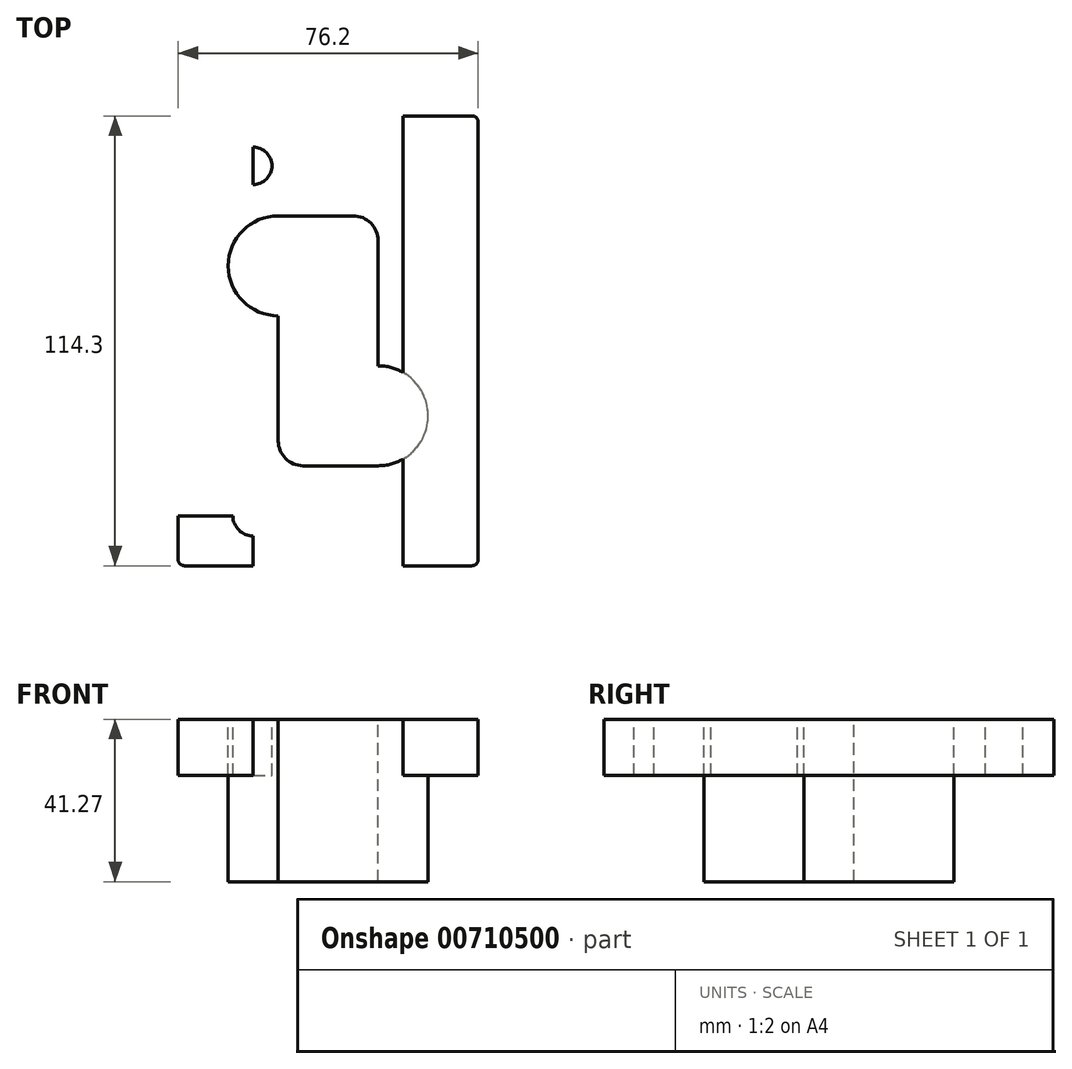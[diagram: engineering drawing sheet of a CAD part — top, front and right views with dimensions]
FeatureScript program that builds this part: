
annotation { "Feature Type Name" : "Feature", "Feature Type Description" : "" }
export const myFeature = defineFeature(function(context is Context, id is Id, definition is map)
    precondition{}
    {
        {
            var Q0;
            Q0=qCreatedBy(makeId("Top.planeOp"),FACE);
            var sketch = newSketch(context, id + "F0", { "sketchPlane" : qUnion([Q0])});
            skLineSegment(sketch, "E0.bottom", {"start": v(12.7, -31.75) * mm, "end": v(-6.35, -31.75) * mm});
            skLineSegment(sketch, "E0.top", {"start": v(6.35, 31.75) * mm, "end": v(-12.7, 31.75) * mm});
            skLineSegment(sketch, "E0.right", {"start": v(-12.7, -25.4) * mm, "end": v(-12.7, 6.35) * mm});
            skPoint(sketch, "E0.middle", {"position": v(0, 0) * mm});
            skArc(sketch, "E1", {"start": v(-12.7, 31.75) * mm, "mid": v(-25.4, 19.05) * mm, "end": v(-12.7, 6.35) * mm});
            skArc(sketch, "E2", {"start": v(12.7, -31.75) * mm, "mid": v(25.4, -19.05) * mm, "end": v(12.7, -6.35) * mm});
            skLineSegment(sketch, "E3.trimOffspring", {"start": v(12.7, -6.35) * mm, "end": v(12.7, 25.4) * mm});
            skPoint(sketch, "E4.start.orphan", {"position": v(-12.7, -19.05) * mm});
            skPoint(sketch, "E5.MirrorCS.end.orphan", {"position": v(12.7, 19.05) * mm});
            skPoint(sketch, "E6.visualSharp", {"position": v(-12.7, -31.75) * mm});
            skArc(sketch, "E6.filletArc", {"start": v(-12.7, -25.4) * mm, "mid": v(-10.84, -29.9) * mm, "end": v(-6.35, -31.75) * mm});
            skPoint(sketch, "E7.visualSharp", {"position": v(12.7, 31.75) * mm});
            skArc(sketch, "E7.filletArc", {"start": v(12.7, 25.4) * mm, "mid": v(10.84, 29.9) * mm, "end": v(6.35, 31.75) * mm});
            skPoint(sketch, "E8.visualSharp", {"position": v(6.35, 19.05) * mm});
            skPoint(sketch, "E9.visualSharp", {"position": v(6.35, -19.05) * mm});
            skSolve(sketch);
        }
        {
            var Q0;
            Q0=makeQuery(id+"F0.imprint","IMPRINT",FACE,{"disambiguationData":[TD([[makeQuery(id+"F0.imprint","IMPRINT",EDGE,{"derivedFrom":sQuery(id+"F0.wireOp",EDGE,"E0.bottom")}),-1.0]])]});
            extrude(context, id + "F1", {"entities" : qUnion([Q0]), "depth" : -41.27 * mm, "offsetDistance" : 25.4 * mm});
        }
        {
            var Q0;
            Q0=makeQuery(id+"F0.imprint","IMPRINT",FACE,{"disambiguationData":[TD([[makeQuery(id+"F0.imprint","IMPRINT",EDGE,{"derivedFrom":sQuery(id+"F0.wireOp",EDGE,"E0.bottom")}),-1.0]])]});
            var sketch = newSketch(context, id + "F2", { "sketchPlane" : qUnion([Q0])});
            skLineSegment(sketch, "E10.bottom", {"start": v(36.51, -57.15) * mm, "end": v(-36.51, -57.15) * mm});
            skLineSegment(sketch, "E10.top", {"start": v(36.51, 57.15) * mm, "end": v(-36.51, 57.15) * mm});
            skLineSegment(sketch, "E10.left", {"start": v(38.1, -55.56) * mm, "end": v(38.1, 55.56) * mm});
            skLineSegment(sketch, "E10.right", {"start": v(-38.1, -55.56) * mm, "end": v(-38.1, 55.56) * mm});
            skPoint(sketch, "E10.middle", {"position": v(0, 0) * mm});
            skLineSegment(sketch, "E11.0.0", {"start": v(6.35, 31.75) * mm, "end": v(-12.7, 31.75) * mm});
            skArc(sketch, "E11.0.1", {"start": v(-12.7, 31.75) * mm, "mid": v(-25.4, 19.05) * mm, "end": v(-12.7, 6.35) * mm});
            skLineSegment(sketch, "E11.0.2", {"start": v(-12.7, 6.35) * mm, "end": v(-12.7, -25.4) * mm});
            skArc(sketch, "E11.0.3", {"start": v(-12.7, -25.4) * mm, "mid": v(-10.84, -29.9) * mm, "end": v(-6.35, -31.75) * mm});
            skLineSegment(sketch, "E11.0.4", {"start": v(-6.35, -31.75) * mm, "end": v(12.7, -31.75) * mm});
            skArc(sketch, "E11.0.5", {"start": v(12.7, -31.75) * mm, "mid": v(25.4, -19.05) * mm, "end": v(12.7, -6.35) * mm});
            skLineSegment(sketch, "E11.0.6", {"start": v(12.7, -6.35) * mm, "end": v(12.7, 25.4) * mm});
            skArc(sketch, "E11.0.7", {"start": v(12.7, 25.4) * mm, "mid": v(10.84, 29.9) * mm, "end": v(6.35, 31.75) * mm});
            skPoint(sketch, "E12.visualSharp", {"position": v(-38.1, 57.15) * mm});
            skArc(sketch, "E12.filletArc", {"start": v(-36.51, 57.15) * mm, "mid": v(-37.64, 56.69) * mm, "end": v(-38.1, 55.56) * mm});
            skPoint(sketch, "E13.visualSharp", {"position": v(38.1, 57.15) * mm});
            skArc(sketch, "E13.filletArc", {"start": v(38.1, 55.56) * mm, "mid": v(37.64, 56.69) * mm, "end": v(36.51, 57.15) * mm});
            skPoint(sketch, "E14.visualSharp", {"position": v(38.1, -57.15) * mm});
            skArc(sketch, "E14.filletArc", {"start": v(36.51, -57.15) * mm, "mid": v(37.64, -56.69) * mm, "end": v(38.1, -55.56) * mm});
            skPoint(sketch, "E15.visualSharp", {"position": v(-38.1, -57.15) * mm});
            skArc(sketch, "E15.filletArc", {"start": v(-38.1, -55.56) * mm, "mid": v(-37.64, -56.69) * mm, "end": v(-36.51, -57.15) * mm});
            skSolve(sketch);
        }
        {
            var Q0;
            Q0=qSketchRegion(id+"F2",true);
            extrude(context, id + "F3", {"entities" : qUnion([Q0]), "operationType" : NewBodyOperationType.ADD, "depth" : -14.29 * mm, "offsetDistance" : 25.4 * mm});
        }
        {
            var Q0;
            Q0=makeQuery(id+"F2.imprint","IMPRINT",FACE,{"disambiguationData":[TD([[makeQuery(id+"F2.imprint","IMPRINT",EDGE,{"derivedFrom":sQuery(id+"F2.wireOp",EDGE,"E10.bottom")}),-1.0]])]});
            var sketch = newSketch(context, id + "F4", { "sketchPlane" : qUnion([Q0])});
            skArc(sketch, "E16.0.0", {"start": v(38.1, 55.56) * mm, "mid": v(37.64, 56.69) * mm, "end": v(36.51, 57.15) * mm});
            skLineSegment(sketch, "E16.0.1", {"start": v(36.51, 57.15) * mm, "end": v(-36.51, 57.15) * mm});
            skArc(sketch, "E16.0.2", {"start": v(-36.51, 57.15) * mm, "mid": v(-37.64, 56.69) * mm, "end": v(-38.1, 55.56) * mm});
            skLineSegment(sketch, "E16.0.3", {"start": v(-38.1, 55.56) * mm, "end": v(-38.1, -55.56) * mm});
            skArc(sketch, "E16.0.4", {"start": v(-38.1, -55.56) * mm, "mid": v(-37.64, -56.69) * mm, "end": v(-36.51, -57.15) * mm});
            skLineSegment(sketch, "E16.0.5", {"start": v(-36.51, -57.15) * mm, "end": v(36.51, -57.15) * mm});
            skArc(sketch, "E16.0.6", {"start": v(36.51, -57.15) * mm, "mid": v(37.64, -56.69) * mm, "end": v(38.1, -55.56) * mm});
            skLineSegment(sketch, "E16.0.7", {"start": v(38.1, -55.56) * mm, "end": v(38.1, 55.56) * mm});
            skLineSegment(sketch, "E17", {"start": v(6.35, 31.75) * mm, "end": v(-12.7, 31.75) * mm});
            skArc(sketch, "E18", {"start": v(-12.7, 31.75) * mm, "mid": v(-25.4, 19.05) * mm, "end": v(-12.7, 6.35) * mm});
            skLineSegment(sketch, "E19", {"start": v(-12.7, -25.4) * mm, "end": v(-12.7, 6.35) * mm});
            skArc(sketch, "E20", {"start": v(-12.7, -25.4) * mm, "mid": v(-10.84, -29.9) * mm, "end": v(-6.35, -31.75) * mm});
            skLineSegment(sketch, "E21", {"start": v(12.7, -31.75) * mm, "end": v(-6.35, -31.75) * mm});
            skArc(sketch, "E22", {"start": v(12.7, -31.75) * mm, "mid": v(25.4, -19.05) * mm, "end": v(12.7, -6.35) * mm});
            skLineSegment(sketch, "E23", {"start": v(12.7, -6.35) * mm, "end": v(12.7, 25.4) * mm});
            skArc(sketch, "E24", {"start": v(12.7, 25.4) * mm, "mid": v(10.84, 29.9) * mm, "end": v(6.35, 31.75) * mm});
            skLineSegment(sketch, "E25", {"start": v(38.1, 44.45) * mm, "end": v(-38.1, 44.45) * mm});
            skLineSegment(sketch, "E26", {"start": v(38.1, -44.45) * mm, "end": v(-38.1, -44.45) * mm});
            skLineSegment(sketch, "E27.direction1", {"start": v(-12.7, -57.15) * mm, "end": v(12.7, -57.15) * mm, "construction": true});
            skLineSegment(sketch, "E28", {"start": v(-19.05, 57.15) * mm, "end": v(-19.05, -57.15) * mm});
            skLineSegment(sketch, "E29", {"start": v(19.05, 57.15) * mm, "end": v(19.05, -57.15) * mm});
            skCircle(sketch, "E30", {"center": v(-19.05, 44.45) * mm, "radius": 4.76 * mm});
            skCircle(sketch, "E31", {"center": v(19.05, -44.45) * mm, "radius": 4.76 * mm});
            skCircle(sketch, "E32", {"center": v(19.05, 44.45) * mm, "radius": 5.16 * mm});
            skCircle(sketch, "E33", {"center": v(-19.05, -44.45) * mm, "radius": 5.16 * mm});
            skSolve(sketch);
        }
        {
            var Q0;
            {var subQ0=sQuery(id+"F4.wireOp",EDGE,"E29");var subQ1=sQuery(id+"F4.wireOp",EDGE,"E25");var subQ2=makeQuery(id+"F4.imprint","INTERSECT",VERTEX,{"derivedFrom":[subQ1,subQ0]});Q0=makeQuery(id+"F4.imprint","IMPRINT",FACE,{"disambiguationData":[TD([[makeQuery(id+"F4.imprint","IMPRINT",EDGE,{"disambiguationData":[TD([[subQ2,-1.0]])],"derivedFrom":subQ1}),1.0]])]});}
            var Q1;
            {var subQ0=sQuery(id+"F4.wireOp",EDGE,"E32");var subQ1=sQuery(id+"F4.wireOp",EDGE,"E25");var subQ2=makeQuery(id+"F4.imprint","INTERSECT",VERTEX,{"disambiguationData":[OD(0.0)],"derivedFrom":[subQ1,subQ0]});Q1=makeQuery(id+"F4.imprint","IMPRINT",FACE,{"disambiguationData":[TD([[makeQuery(id+"F4.imprint","IMPRINT",EDGE,{"disambiguationData":[TD([[subQ2,-1.0]])],"derivedFrom":subQ1}),-1.0]])]});}
            var Q2;
            {var subQ0=sQuery(id+"F4.wireOp",EDGE,"E29");var subQ1=sQuery(id+"F4.wireOp",EDGE,"E25");var subQ2=makeQuery(id+"F4.imprint","INTERSECT",VERTEX,{"derivedFrom":[subQ1,subQ0]});Q2=makeQuery(id+"F4.imprint","IMPRINT",FACE,{"disambiguationData":[TD([[makeQuery(id+"F4.imprint","IMPRINT",EDGE,{"disambiguationData":[TD([[subQ2,-1.0]])],"derivedFrom":subQ1}),-1.0]])]});}
            var Q3;
            {var subQ0=sQuery(id+"F4.wireOp",EDGE,"E32");var subQ1=sQuery(id+"F4.wireOp",EDGE,"E25");var subQ2=makeQuery(id+"F4.imprint","INTERSECT",VERTEX,{"disambiguationData":[OD(0.0)],"derivedFrom":[subQ1,subQ0]});Q3=makeQuery(id+"F4.imprint","IMPRINT",FACE,{"disambiguationData":[TD([[makeQuery(id+"F4.imprint","IMPRINT",EDGE,{"disambiguationData":[TD([[subQ2,-1.0]])],"derivedFrom":subQ1}),1.0]])]});}
            var Q4;
            {var subQ0=sQuery(id+"F4.wireOp",EDGE,"E33");var subQ1=sQuery(id+"F4.wireOp",EDGE,"E26");var subQ2=makeQuery(id+"F4.imprint","INTERSECT",VERTEX,{"disambiguationData":[OD(0.0)],"derivedFrom":[subQ1,subQ0]});Q4=makeQuery(id+"F4.imprint","IMPRINT",FACE,{"disambiguationData":[TD([[makeQuery(id+"F4.imprint","IMPRINT",EDGE,{"disambiguationData":[TD([[subQ2,-1.0]])],"derivedFrom":subQ1}),-1.0]])]});}
            var Q5;
            {var subQ0=sQuery(id+"F4.wireOp",EDGE,"E33");var subQ1=sQuery(id+"F4.wireOp",EDGE,"E26");var subQ2=makeQuery(id+"F4.imprint","INTERSECT",VERTEX,{"disambiguationData":[OD(0.0)],"derivedFrom":[subQ1,subQ0]});Q5=makeQuery(id+"F4.imprint","IMPRINT",FACE,{"disambiguationData":[TD([[makeQuery(id+"F4.imprint","IMPRINT",EDGE,{"disambiguationData":[TD([[subQ2,-1.0]])],"derivedFrom":subQ1}),1.0]])]});}
            var Q6;
            {var subQ0=sQuery(id+"F4.wireOp",EDGE,"E28");var subQ1=sQuery(id+"F4.wireOp",EDGE,"E26");var subQ2=makeQuery(id+"F4.imprint","INTERSECT",VERTEX,{"derivedFrom":[subQ1,subQ0]});Q6=makeQuery(id+"F4.imprint","IMPRINT",FACE,{"disambiguationData":[TD([[makeQuery(id+"F4.imprint","IMPRINT",EDGE,{"disambiguationData":[TD([[subQ2,-1.0]])],"derivedFrom":subQ1}),1.0]])]});}
            var Q7;
            {var subQ0=sQuery(id+"F4.wireOp",EDGE,"E28");var subQ1=sQuery(id+"F4.wireOp",EDGE,"E26");var subQ2=makeQuery(id+"F4.imprint","INTERSECT",VERTEX,{"derivedFrom":[subQ1,subQ0]});Q7=makeQuery(id+"F4.imprint","IMPRINT",FACE,{"disambiguationData":[TD([[makeQuery(id+"F4.imprint","IMPRINT",EDGE,{"disambiguationData":[TD([[subQ2,-1.0]])],"derivedFrom":subQ1}),-1.0]])]});}
            var Q8;
            {var subQ0=sQuery(id+"F4.wireOp",EDGE,"E30");var subQ1=sQuery(id+"F4.wireOp",EDGE,"E25");var subQ2=makeQuery(id+"F4.imprint","INTERSECT",VERTEX,{"disambiguationData":[OD(0.0)],"derivedFrom":[subQ1,subQ0]});Q8=makeQuery(id+"F4.imprint","IMPRINT",FACE,{"disambiguationData":[TD([[makeQuery(id+"F4.imprint","IMPRINT",EDGE,{"disambiguationData":[TD([[subQ2,-1.0]])],"derivedFrom":subQ1}),1.0]])]});}
            var Q9;
            {var subQ0=sQuery(id+"F4.wireOp",EDGE,"E30");var subQ1=sQuery(id+"F4.wireOp",EDGE,"E25");var subQ2=makeQuery(id+"F4.imprint","INTERSECT",VERTEX,{"disambiguationData":[OD(0.0)],"derivedFrom":[subQ1,subQ0]});Q9=makeQuery(id+"F4.imprint","IMPRINT",FACE,{"disambiguationData":[TD([[makeQuery(id+"F4.imprint","IMPRINT",EDGE,{"disambiguationData":[TD([[subQ2,-1.0]])],"derivedFrom":subQ1}),-1.0]])]});}
            var Q10;
            {var subQ0=sQuery(id+"F4.wireOp",EDGE,"E28");var subQ1=sQuery(id+"F4.wireOp",EDGE,"E25");var subQ2=makeQuery(id+"F4.imprint","INTERSECT",VERTEX,{"derivedFrom":[subQ1,subQ0]});Q10=makeQuery(id+"F4.imprint","IMPRINT",FACE,{"disambiguationData":[TD([[makeQuery(id+"F4.imprint","IMPRINT",EDGE,{"disambiguationData":[TD([[subQ2,-1.0]])],"derivedFrom":subQ1}),-1.0]])]});}
            var Q11;
            {var subQ0=sQuery(id+"F4.wireOp",EDGE,"E28");var subQ1=sQuery(id+"F4.wireOp",EDGE,"E25");var subQ2=makeQuery(id+"F4.imprint","INTERSECT",VERTEX,{"derivedFrom":[subQ1,subQ0]});Q11=makeQuery(id+"F4.imprint","IMPRINT",FACE,{"disambiguationData":[TD([[makeQuery(id+"F4.imprint","IMPRINT",EDGE,{"disambiguationData":[TD([[subQ2,-1.0]])],"derivedFrom":subQ1}),1.0]])]});}
            var Q12;
            {var subQ0=sQuery(id+"F4.wireOp",EDGE,"E31");var subQ1=sQuery(id+"F4.wireOp",EDGE,"E26");var subQ2=makeQuery(id+"F4.imprint","INTERSECT",VERTEX,{"disambiguationData":[OD(0.0)],"derivedFrom":[subQ1,subQ0]});Q12=makeQuery(id+"F4.imprint","IMPRINT",FACE,{"disambiguationData":[TD([[makeQuery(id+"F4.imprint","IMPRINT",EDGE,{"disambiguationData":[TD([[subQ2,-1.0]])],"derivedFrom":subQ1}),-1.0]])]});}
            var Q13;
            {var subQ0=sQuery(id+"F4.wireOp",EDGE,"E29");var subQ1=sQuery(id+"F4.wireOp",EDGE,"E26");var subQ2=makeQuery(id+"F4.imprint","INTERSECT",VERTEX,{"derivedFrom":[subQ1,subQ0]});Q13=makeQuery(id+"F4.imprint","IMPRINT",FACE,{"disambiguationData":[TD([[makeQuery(id+"F4.imprint","IMPRINT",EDGE,{"disambiguationData":[TD([[subQ2,-1.0]])],"derivedFrom":subQ1}),-1.0]])]});}
            var Q14;
            {var subQ0=sQuery(id+"F4.wireOp",EDGE,"E29");var subQ1=sQuery(id+"F4.wireOp",EDGE,"E26");var subQ2=makeQuery(id+"F4.imprint","INTERSECT",VERTEX,{"derivedFrom":[subQ1,subQ0]});Q14=makeQuery(id+"F4.imprint","IMPRINT",FACE,{"disambiguationData":[TD([[makeQuery(id+"F4.imprint","IMPRINT",EDGE,{"disambiguationData":[TD([[subQ2,-1.0]])],"derivedFrom":subQ1}),1.0]])]});}
            var Q15;
            {var subQ0=sQuery(id+"F4.wireOp",EDGE,"E31");var subQ1=sQuery(id+"F4.wireOp",EDGE,"E26");var subQ2=makeQuery(id+"F4.imprint","INTERSECT",VERTEX,{"disambiguationData":[OD(0.0)],"derivedFrom":[subQ1,subQ0]});Q15=makeQuery(id+"F4.imprint","IMPRINT",FACE,{"disambiguationData":[TD([[makeQuery(id+"F4.imprint","IMPRINT",EDGE,{"disambiguationData":[TD([[subQ2,-1.0]])],"derivedFrom":subQ1}),1.0]])]});}
            extrude(context, id + "F5", {"entities" : qUnion([Q0, Q1, Q2, Q3, Q4, Q5, Q6, Q7, Q8, Q9, Q10, Q11, Q12, Q13, Q14, Q15]), "operationType" : NewBodyOperationType.REMOVE, "oppositeDirection" : true, "depth" : 14.29 * mm, "offsetDistance" : 25.4 * mm});
        }
    });
